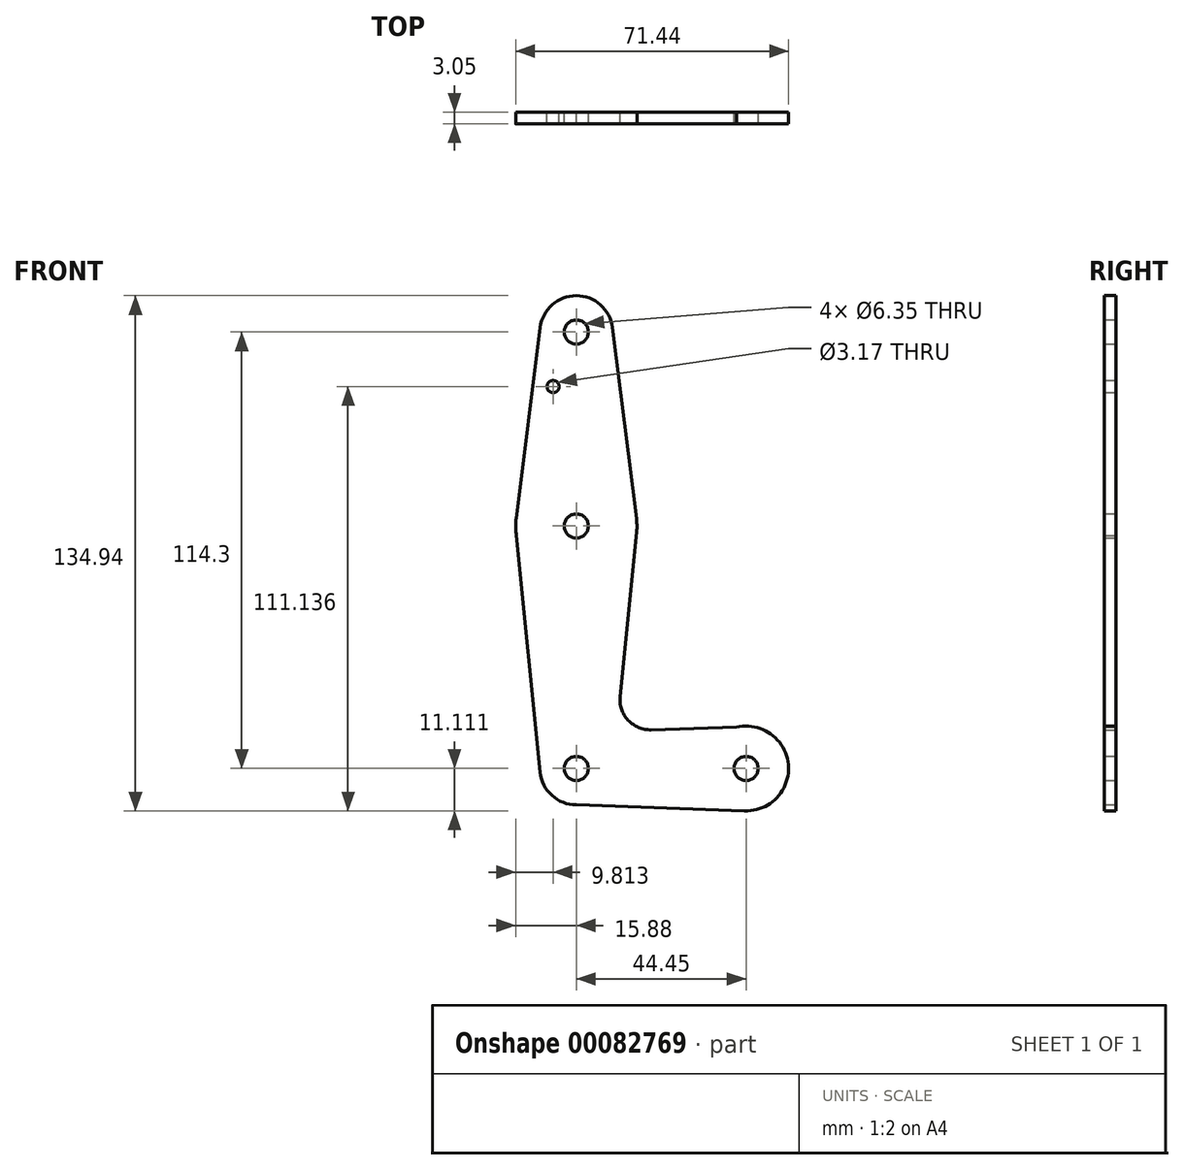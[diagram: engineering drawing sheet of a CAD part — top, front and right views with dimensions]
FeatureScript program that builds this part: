
annotation { "Feature Type Name" : "Feature", "Feature Type Description" : "" }
export const myFeature = defineFeature(function(context is Context, id is Id, definition is map)
    precondition{}
    {
        {
            var Q0;
            Q0=qCreatedBy(makeId("Front.planeOp"),FACE);
            var sketch = newSketch(context, id + "F0", { "sketchPlane" : qUnion([Q0])});
            skLineSegment(sketch, "E0", {"start": v(-44.45, 72.61) * mm, "end": v(-44.45, -41.69) * mm, "construction": true});
            skLineSegment(sketch, "E1", {"start": v(-44.45, -41.69) * mm, "end": v(0, -41.69) * mm, "construction": true});
            skCircle(sketch, "E2", {"center": v(-44.45, 72.61) * mm, "radius": 9.53 * mm});
            skCircle(sketch, "E3", {"center": v(-44.45, -41.69) * mm, "radius": 9.53 * mm});
            skCircle(sketch, "E4", {"center": v(0, -41.69) * mm, "radius": 11.11 * mm});
            skCircle(sketch, "E5", {"center": v(-44.45, 21.81) * mm, "radius": 15.88 * mm});
            skLineSegment(sketch, "E6", {"start": v(-53.9, 73.8) * mm, "end": v(-60.2, 23.8) * mm});
            skLineSegment(sketch, "E7", {"start": v(-35, 73.8) * mm, "end": v(-28.7, 23.8) * mm});
            skLineSegment(sketch, "E8", {"start": v(-60.13, 19.32) * mm, "end": v(-53.93, -42.64) * mm});
            skLineSegment(sketch, "E9", {"start": v(-28.65, 20.22) * mm, "end": v(-32.98, -22.81) * mm});
            skLineSegment(sketch, "E10", {"start": v(-24.82, -31.56) * mm, "end": v(1.85, -30.73) * mm});
            skLineSegment(sketch, "E11", {"start": v(-44.38, -51.21) * mm, "end": v(0, -52.8) * mm});
            skCircle(sketch, "E12", {"center": v(-44.45, 72.61) * mm, "radius": 3.18 * mm});
            skCircle(sketch, "E13", {"center": v(-44.45, 21.81) * mm, "radius": 3.18 * mm});
            skCircle(sketch, "E14", {"center": v(-44.45, -41.69) * mm, "radius": 3.18 * mm});
            skCircle(sketch, "E15", {"center": v(0, -41.69) * mm, "radius": 3.18 * mm});
            skArc(sketch, "E16.filletArc", {"start": v(-32.98, -22.81) * mm, "mid": v(-30.88, -29.03) * mm, "end": v(-24.82, -31.56) * mm});
            skCircle(sketch, "E17", {"center": v(-50.52, 58.34) * mm, "radius": 1.59 * mm});
            skSolve(sketch);
        }
        {
            var Q0;
            Q0 = qSketchRegion(id + "F0", true);
            extrude(context, id + "F1", {"entities" : qUnion([Q0]), "depth" : 3.05 * mm});
        }
    });
